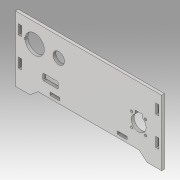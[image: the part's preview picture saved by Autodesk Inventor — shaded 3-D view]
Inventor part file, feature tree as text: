
AUTODESK INVENTOR PART (.ipt)
format: ipt  version: 2019.3 (Build 233278000, 278)  size: 199,168 bytes
history: native  units: mm
features: extrude x3, sketch x3
ambient origin geometry x8: Origin, YZ Plane, XZ Plane, XY Plane, X Axis, Y Axis, Z Axis, Center Point
bodies: Solid1 (feature_tree)
feature tree (6):
  extrude  "Extrusion1"  Depth=10.0mm
  extrude  "Extrusion2"  Depth=10.0mm
  extrude  "Extrusion3"  Depth=36.0mm
  sketch  "Sketch1"  dims[d0=3.0mm d1=10.0mm]
  sketch  "Sketch2"  dims[d2=60.0mm d3=10.0mm]
  sketch  "Sketch3"  dims[d4=152.0mm d5=36.0mm d6=36.0mm d7=3.1mm d8=10.0mm d9=20.0mm d10=5.0mm d11=10.0mm d12=3.0mm d13=3.0mm d14=3.0mm d15=15.0mm d16=15.0mm d17=105.0mm d18=3.0mm d19=0.0mm d21=16.0mm d24=10.0mm d25=0.0mm d26=22.4mm d29=1.0mm d30=6.58mm d31=9.83mm d32=15.5mm d33=7.0mm d34=18.0mm d35=2.5mm d36=17.0mm d37=17.0mm d38=10.253048mm d39=10.253048mm d40=10.253048mm d41=17.75mm d42=10.0mm d43=17.75mm d44=12.0mm d45=20.0mm d46=25.0mm d47=20.0mm d48=2.0mm d49=10.8mm d50=20.0mm d51=10.050126mm d52=10.0mm d53=0.0mm]
